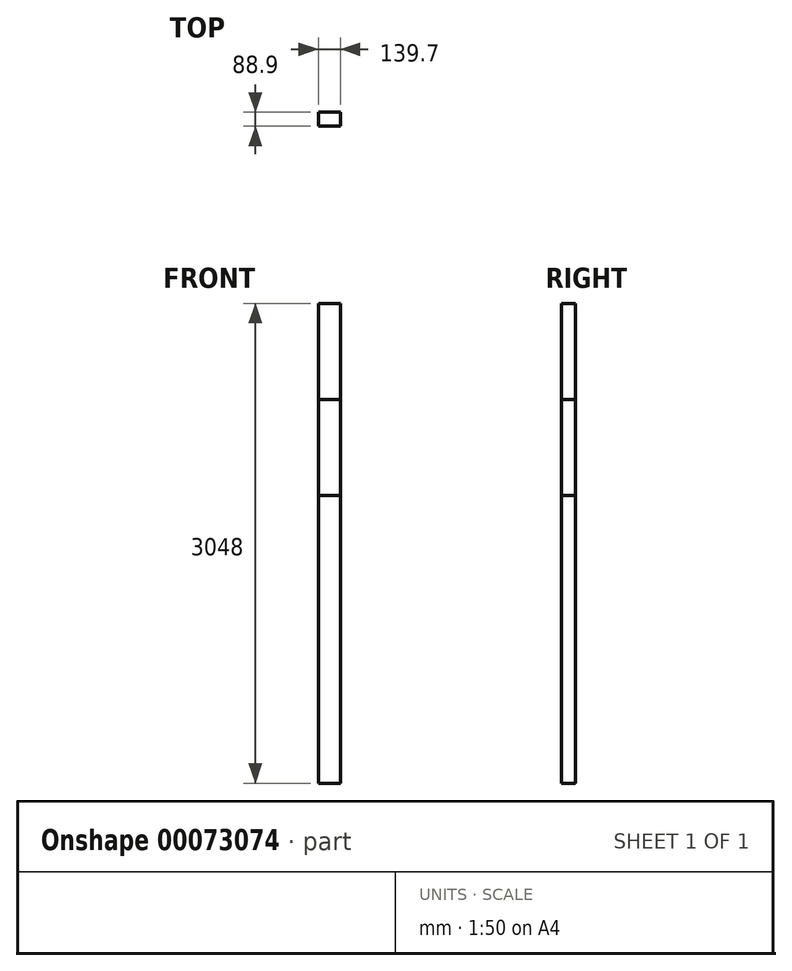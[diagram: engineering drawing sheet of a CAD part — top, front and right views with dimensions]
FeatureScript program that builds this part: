
annotation { "Feature Type Name" : "Feature", "Feature Type Description" : "" }
export const myFeature = defineFeature(function(context is Context, id is Id, definition is map)
    precondition{}
    {
        {
            var Q0;
            Q0=qCreatedBy(makeId("Top.planeOp"),FACE);
            var sketch = newSketch(context, id + "F0", { "sketchPlane" : qUnion([Q0])});
            skLineSegment(sketch, "E0.bottom", {"start": v(-147.88, 17.65) * mm, "end": v(-8.18, 17.65) * mm});
            skLineSegment(sketch, "E0.top", {"start": v(-147.88, -71.25) * mm, "end": v(-8.18, -71.25) * mm});
            skLineSegment(sketch, "E0.left", {"start": v(-147.88, 17.65) * mm, "end": v(-147.88, -71.25) * mm});
            skLineSegment(sketch, "E0.right", {"start": v(-8.18, 17.65) * mm, "end": v(-8.18, -71.25) * mm});
            skSolve(sketch);
        }
        {
            var Q0;
            Q0 = qSketchRegion(id + "F0", true);
            extrude(context, id + "F1", {"entities" : qUnion([Q0]), "depth" : 1828.8 * mm});
        }
        {
            var Q0;
            Q0=makeQuery(id+"F0.imprint","IMPRINT",FACE,{"disambiguationData":[TD([[makeQuery(id+"F0.imprint","IMPRINT",EDGE,{"derivedFrom":sQuery(id+"F0.wireOp",EDGE,"E0.bottom")}),-1.0]])]});
            extrude(context, id + "F2", {"entities" : qUnion([Q0]), "depth" : 2438.4 * mm});
        }
        {
            var Q0;
            Q0=makeQuery(id+"F0.imprint","IMPRINT",FACE,{"disambiguationData":[TD([[makeQuery(id+"F0.imprint","IMPRINT",EDGE,{"derivedFrom":sQuery(id+"F0.wireOp",EDGE,"E0.bottom")}),-1.0]])]});
            extrude(context, id + "F3", {"entities" : qUnion([Q0]), "depth" : 3048 * mm});
        }
    });
